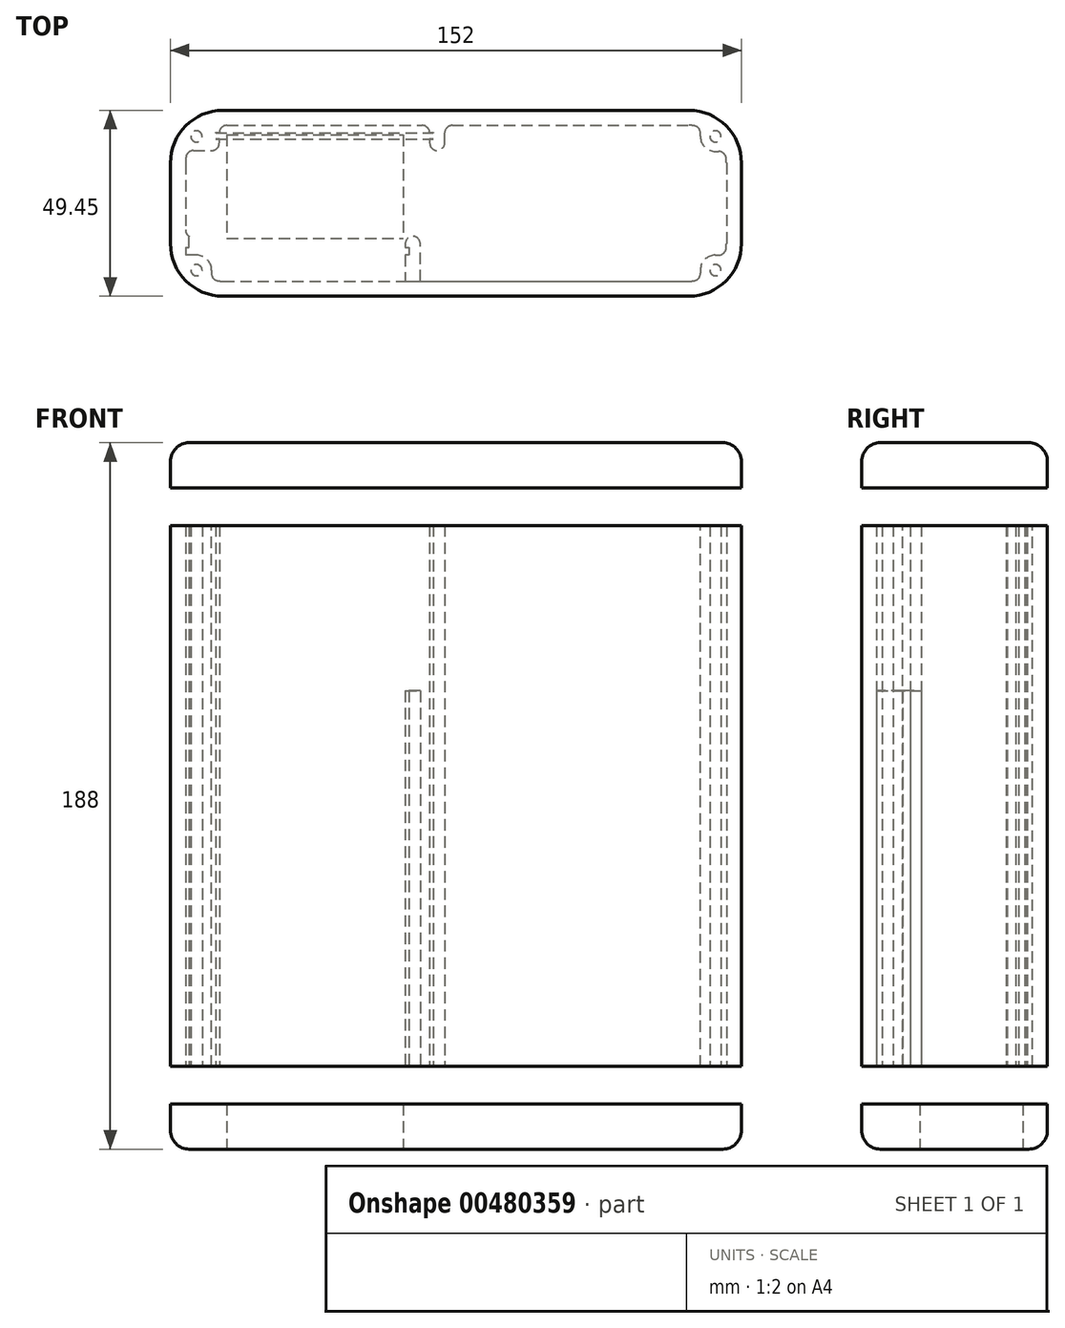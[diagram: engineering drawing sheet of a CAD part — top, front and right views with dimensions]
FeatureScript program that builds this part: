
annotation { "Feature Type Name" : "Feature", "Feature Type Description" : "" }
export const myFeature = defineFeature(function(context is Context, id is Id, definition is map)
    precondition{}
    {
        {
            var Q0;
            Q0=qCreatedBy(makeId("Top.planeOp"),FACE);
            var sketch = newSketch(context, id + "F0", { "sketchPlane" : qUnion([Q0])});
            skLineSegment(sketch, "E0.bottom", {"start": v(-110.78, -14.87) * mm, "end": v(-51.28, -14.87) * mm, "construction": true});
            skLineSegment(sketch, "E0.top", {"start": v(-110.78, -16.67) * mm, "end": v(-51.28, -16.67) * mm, "construction": true});
            skLineSegment(sketch, "E0.left", {"start": v(-110.78, -14.87) * mm, "end": v(-110.78, -16.67) * mm});
            skLineSegment(sketch, "E0.right", {"start": v(-51.28, -14.87) * mm, "end": v(-51.28, -16.67) * mm});
            skLineSegment(sketch, "E1.bottom", {"start": v(-100.78, 17.75) * mm, "end": v(23.22, 17.75) * mm});
            skLineSegment(sketch, "E1.top", {"start": v(-100.78, -23.7) * mm, "end": v(23.22, -23.7) * mm});
            skLineSegment(sketch, "E1.left", {"start": v(-110.78, 7.75) * mm, "end": v(-110.78, -13.7) * mm});
            skLineSegment(sketch, "E1.right", {"start": v(33.22, 7.75) * mm, "end": v(33.22, -13.7) * mm});
            skPoint(sketch, "E2", {"position": v(-38.78, -23.7) * mm});
            skPoint(sketch, "E3.visualSharp", {"position": v(-110.78, 17.75) * mm});
            skArc(sketch, "E3.filletArc", {"start": v(-100.78, 17.75) * mm, "mid": v(-107.85, 14.83) * mm, "end": v(-110.78, 7.75) * mm});
            skPoint(sketch, "E4.visualSharp", {"position": v(33.22, 17.75) * mm});
            skArc(sketch, "E4.filletArc", {"start": v(33.22, 7.75) * mm, "mid": v(30.29, 14.83) * mm, "end": v(23.22, 17.75) * mm});
            skPoint(sketch, "E5.visualSharp", {"position": v(33.22, -23.7) * mm});
            skArc(sketch, "E5.filletArc", {"start": v(23.22, -23.7) * mm, "mid": v(30.29, -20.77) * mm, "end": v(33.22, -13.7) * mm});
            skPoint(sketch, "E6.visualSharp", {"position": v(-110.78, -23.7) * mm});
            skArc(sketch, "E6.filletArc", {"start": v(-110.78, -13.7) * mm, "mid": v(-107.85, -20.77) * mm, "end": v(-100.78, -23.7) * mm});
            skLineSegment(sketch, "E7.0", {"start": v(-100.78, 21.75) * mm, "end": v(23.22, 21.75) * mm});
            skArc(sketch, "E7.1", {"start": v(37.22, 7.75) * mm, "mid": v(33.12, 17.65) * mm, "end": v(23.22, 21.75) * mm});
            skArc(sketch, "E7.2", {"start": v(-100.78, 21.75) * mm, "mid": v(-110.68, 17.65) * mm, "end": v(-114.78, 7.75) * mm});
            skLineSegment(sketch, "E7.3", {"start": v(37.22, 7.75) * mm, "end": v(37.22, -13.7) * mm});
            skLineSegment(sketch, "E7.4", {"start": v(-114.78, 7.75) * mm, "end": v(-114.78, -13.7) * mm});
            skArc(sketch, "E7.5", {"start": v(-114.78, -13.7) * mm, "mid": v(-110.68, -23.6) * mm, "end": v(-100.78, -27.7) * mm});
            skLineSegment(sketch, "E7.6", {"start": v(-100.78, -27.7) * mm, "end": v(23.22, -27.7) * mm});
            skArc(sketch, "E7.7", {"start": v(23.22, -27.7) * mm, "mid": v(33.12, -23.6) * mm, "end": v(37.22, -13.7) * mm});
            skPoint(sketch, "E8", {"position": v(-38.78, -12.34) * mm});
            skPoint(sketch, "E9.visualSharp", {"position": v(-107.28, -12.34) * mm});
            skPoint(sketch, "E10.visualSharp", {"position": v(-107.28, -52.34) * mm});
            skPoint(sketch, "E11.visualSharp", {"position": v(29.72, -52.34) * mm});
            skCircle(sketch, "E12", {"center": v(-107.85, 14.83) * mm, "radius": 4 * mm});
            skLineSegment(sketch, "E13", {"start": v(-100.78, 7.75) * mm, "end": v(-110.78, 17.75) * mm, "construction": true});
            skCircle(sketch, "E14", {"center": v(30.29, -20.77) * mm, "radius": 4 * mm});
            skLineSegment(sketch, "E15", {"start": v(23.22, -13.7) * mm, "end": v(33.22, -23.7) * mm, "construction": true});
            skCircle(sketch, "E16", {"center": v(-107.85, -20.77) * mm, "radius": 4 * mm});
            skLineSegment(sketch, "E17", {"start": v(-100.78, -13.7) * mm, "end": v(-110.78, -23.7) * mm, "construction": true});
            skLineSegment(sketch, "E18.bottom", {"start": v(-102.78, 15.75) * mm, "end": v(-44.78, 15.75) * mm});
            skLineSegment(sketch, "E18.top", {"start": v(-102.78, 14.15) * mm, "end": v(-44.78, 14.15) * mm});
            skLineSegment(sketch, "E18.left", {"start": v(-102.78, 15.75) * mm, "end": v(-102.78, 14.15) * mm});
            skLineSegment(sketch, "E18.right", {"start": v(-44.78, 15.75) * mm, "end": v(-44.78, 14.15) * mm});
            skLineSegment(sketch, "E19", {"start": v(-45.78, 17.75) * mm, "end": v(-45.78, 15.85) * mm});
            skLineSegment(sketch, "E20", {"start": v(-45.78, 15.85) * mm, "end": v(-44.78, 15.85) * mm});
            skLineSegment(sketch, "E21", {"start": v(-44.78, 15.85) * mm, "end": v(-44.78, 14.05) * mm});
            skLineSegment(sketch, "E22", {"start": v(-44.78, 14.05) * mm, "end": v(-45.78, 14.05) * mm});
            skLineSegment(sketch, "E23", {"start": v(-45.78, 14.05) * mm, "end": v(-45.78, 11.05) * mm});
            skLineSegment(sketch, "E24", {"start": v(-45.78, 11.05) * mm, "end": v(-41.78, 11.05) * mm});
            skLineSegment(sketch, "E25", {"start": v(-41.78, 11.05) * mm, "end": v(-41.78, 17.75) * mm});
            skPoint(sketch, "E26", {"position": v(-44.78, 14.95) * mm});
            skLineSegment(sketch, "E27", {"start": v(-110.78, 11.05) * mm, "end": v(-101.78, 11.05) * mm});
            skLineSegment(sketch, "E28", {"start": v(-101.78, 11.05) * mm, "end": v(-101.78, 14.05) * mm});
            skLineSegment(sketch, "E29", {"start": v(-101.78, 14.05) * mm, "end": v(-110.78, 14.05) * mm});
            skLineSegment(sketch, "E30", {"start": v(-107.85, -16.77) * mm, "end": v(-110.3, -16.77) * mm});
            skLineSegment(sketch, "E31", {"start": v(-103.85, -20.77) * mm, "end": v(-103.85, -23.22) * mm});
            skLineSegment(sketch, "E32", {"start": v(30.29, -16.77) * mm, "end": v(32.74, -16.77) * mm});
            skLineSegment(sketch, "E33", {"start": v(26.29, -20.77) * mm, "end": v(26.29, -23.22) * mm});
            skLineSegment(sketch, "E34", {"start": v(-110.78, -14.77) * mm, "end": v(-109.78, -14.77) * mm});
            skLineSegment(sketch, "E35", {"start": v(-109.78, -14.77) * mm, "end": v(-109.78, -11.77) * mm});
            skLineSegment(sketch, "E36", {"start": v(-109.78, -11.77) * mm, "end": v(-110.78, -11.77) * mm});
            skLineSegment(sketch, "E37", {"start": v(-110.78, -16.77) * mm, "end": v(-109.78, -16.77) * mm});
            skLineSegment(sketch, "E38", {"start": v(-51.28, -9.75) * mm, "end": v(-51.28, -11.75) * mm});
            skCircle(sketch, "E39", {"center": v(30.29, 14.83) * mm, "radius": 4 * mm});
            skCircle(sketch, "E40", {"center": v(30.29, 14.83) * mm, "radius": 1.5 * mm});
            skCircle(sketch, "E41", {"center": v(-107.85, 14.83) * mm, "radius": 1.5 * mm});
            skCircle(sketch, "E42", {"center": v(-107.85, -20.77) * mm, "radius": 1.5 * mm});
            skCircle(sketch, "E43", {"center": v(30.29, -20.77) * mm, "radius": 1.5 * mm});
            skLineSegment(sketch, "E44", {"start": v(33.22, 17.75) * mm, "end": v(23.22, 7.75) * mm, "construction": true});
            skLineSegment(sketch, "E45", {"start": v(-48.28, -23.7) * mm, "end": v(-48.28, -11.77) * mm});
            skLineSegment(sketch, "E46", {"start": v(-48.28, -11.77) * mm, "end": v(-52.28, -11.77) * mm});
            skLineSegment(sketch, "E47", {"start": v(-52.28, -11.77) * mm, "end": v(-52.28, -14.77) * mm});
            skLineSegment(sketch, "E48", {"start": v(-52.28, -14.77) * mm, "end": v(-51.28, -14.77) * mm});
            skLineSegment(sketch, "E49", {"start": v(-51.28, -14.77) * mm, "end": v(-51.28, -16.77) * mm});
            skLineSegment(sketch, "E50", {"start": v(-51.28, -16.77) * mm, "end": v(-52.28, -16.77) * mm});
            skLineSegment(sketch, "E51", {"start": v(-52.28, -16.77) * mm, "end": v(-52.28, -23.7) * mm});
            skLineSegment(sketch, "E52", {"start": v(26.29, 14.83) * mm, "end": v(26.29, 17.27) * mm});
            skLineSegment(sketch, "E53", {"start": v(30.29, 10.83) * mm, "end": v(32.74, 10.83) * mm});
            skLineSegment(sketch, "E54", {"start": v(-102.78, 14.05) * mm, "end": v(-102.78, 15.85) * mm});
            skLineSegment(sketch, "E55", {"start": v(-110.78, -14.77) * mm, "end": v(-110.78, -16.77) * mm});
            skLineSegment(sketch, "E56", {"start": v(-101.78, 15.85) * mm, "end": v(-101.78, 17.7) * mm});
            skLineSegment(sketch, "E57", {"start": v(-102.78, 15.85) * mm, "end": v(-101.78, 15.85) * mm});
            skSolve(sketch);
        }
        {
            var Q0;
            {var subQ9=sQuery(id+"F0.wireOp",EDGE,"E7.0");Q0=makeQuery(id+"F0.imprint","IMPRINT",FACE,{"disambiguationData":[TD([[makeQuery(id+"F0.imprint","IMPRINT",EDGE,{"derivedFrom":subQ9}),-1.0]])]});}
            var Q1;
            {var subQ0=sQuery(id+"F0.wireOp",EDGE,"E12");var subQ2=sQuery(id+"F0.wireOp",EDGE,"E3.filletArc");var subQ3=makeQuery(id+"F0.imprint","INTERSECT",VERTEX,{"disambiguationData":[OD(0.0)],"derivedFrom":[subQ2,subQ0]});Q1=makeQuery(id+"F0.imprint","IMPRINT",FACE,{"disambiguationData":[TD([[makeQuery(id+"F0.imprint","IMPRINT",EDGE,{"disambiguationData":[TD([[subQ3,-1.0]])],"derivedFrom":subQ2}),-1.0]])]});}
            var Q2;
            {var subQ0=sQuery(id+"F0.wireOp",EDGE,"2W4B9iu8-6ltF-Vtcw-TABt-Mn2br8Ru9iya");Q2=makeQuery(id+"F0.imprint","IMPRINT",FACE,{"disambiguationData":[TD([[makeQuery(id+"F0.imprint","IMPRINT",EDGE,{"derivedFrom":subQ0}),1.0]])]});}
            var Q3;
            {var subQ0=sQuery(id+"F0.wireOp",EDGE,"E12");var subQ2=sQuery(id+"F0.wireOp",EDGE,"E3.filletArc");var subQ8=makeQuery(id+"F0.imprint","INTERSECT",VERTEX,{"disambiguationData":[OD(0.0)],"derivedFrom":[subQ2,subQ0]});Q3=makeQuery(id+"F0.imprint","IMPRINT",FACE,{"disambiguationData":[TD([[makeQuery(id+"F0.imprint","IMPRINT",EDGE,{"disambiguationData":[TD([[subQ8,-1.0]])],"derivedFrom":subQ2}),1.0]])]});}
            var Q4;
            {var subQ0=sQuery(id+"F0.wireOp",EDGE,"aaEoFGYO-67Ow-w31H-SEpQ-SyWXDBz15Rrq");Q4=makeQuery(id+"F0.imprint","IMPRINT",FACE,{"disambiguationData":[TD([[makeQuery(id+"F0.imprint","IMPRINT",EDGE,{"derivedFrom":subQ0}),-1.0]])]});}
            var Q5;
            {var subQ0=sQuery(id+"F0.wireOp",EDGE,"E7.3");Q5=makeQuery(id+"F0.imprint","IMPRINT",FACE,{"disambiguationData":[TD([[makeQuery(id+"F0.imprint","IMPRINT",EDGE,{"derivedFrom":subQ0}),-1.0]])]});}
            var Q6;
            {var subQ0=sQuery(id+"F0.wireOp",EDGE,"E14");var subQ2=sQuery(id+"F0.wireOp",EDGE,"E5.filletArc");var subQ3=makeQuery(id+"F0.imprint","INTERSECT",VERTEX,{"disambiguationData":[OD(0.0)],"derivedFrom":[subQ2,subQ0]});Q6=makeQuery(id+"F0.imprint","IMPRINT",FACE,{"disambiguationData":[TD([[makeQuery(id+"F0.imprint","IMPRINT",EDGE,{"disambiguationData":[TD([[subQ3,-1.0]])],"derivedFrom":subQ2}),-1.0]])]});}
            var Q7;
            {var subQ1=sQuery(id+"F0.wireOp",EDGE,"E14");var subQ6=sQuery(id+"F0.wireOp",EDGE,"E5.filletArc");var subQ7=makeQuery(id+"F0.imprint","INTERSECT",VERTEX,{"disambiguationData":[OD(0.0)],"derivedFrom":[subQ6,subQ1]});Q7=makeQuery(id+"F0.imprint","IMPRINT",FACE,{"disambiguationData":[TD([[makeQuery(id+"F0.imprint","IMPRINT",EDGE,{"disambiguationData":[TD([[subQ7,-1.0]])],"derivedFrom":subQ6}),1.0]])]});}
            var Q8;
            {var subQ9=sQuery(id+"F0.wireOp",EDGE,"E1.top");Q8=makeQuery(id+"F0.imprint","IMPRINT",FACE,{"disambiguationData":[TD([[makeQuery(id+"F0.imprint","IMPRINT",EDGE,{"derivedFrom":subQ9}),-1.0]])]});}
            var Q9;
            {var subQ0=sQuery(id+"F0.wireOp",EDGE,"E16");var subQ2=sQuery(id+"F0.wireOp",EDGE,"E6.filletArc");var subQ3=makeQuery(id+"F0.imprint","INTERSECT",VERTEX,{"disambiguationData":[OD(0.0)],"derivedFrom":[subQ2,subQ0]});Q9=makeQuery(id+"F0.imprint","IMPRINT",FACE,{"disambiguationData":[TD([[makeQuery(id+"F0.imprint","IMPRINT",EDGE,{"disambiguationData":[TD([[subQ3,-1.0]])],"derivedFrom":subQ2}),-1.0]])]});}
            var Q10;
            {var subQ0=sQuery(id+"F0.wireOp",EDGE,"E16");var subQ1=sQuery(id+"F0.wireOp",EDGE,"E6.filletArc");var subQ2=makeQuery(id+"F0.imprint","INTERSECT",VERTEX,{"disambiguationData":[OD(0.0)],"derivedFrom":[subQ1,subQ0]});Q10=makeQuery(id+"F0.imprint","IMPRINT",FACE,{"disambiguationData":[TD([[makeQuery(id+"F0.imprint","IMPRINT",EDGE,{"disambiguationData":[TD([[subQ2,-1.0]])],"derivedFrom":subQ1}),1.0]])]});}
            var Q11;
            {var subQ7=sQuery(id+"F0.wireOp",EDGE,"ttZv5H3B-eX0E-SKTf-zCUi-YB3ncVsOdNPo");Q11=makeQuery(id+"F0.imprint","IMPRINT",FACE,{"disambiguationData":[TD([[makeQuery(id+"F0.imprint","IMPRINT",EDGE,{"derivedFrom":subQ7}),-1.0]])]});}
            var Q12;
            {var subQ0=sQuery(id+"F0.wireOp",EDGE,"kMDQpda2-fsvu-s4YW-gm7I-p9UYXz8PP6ZB");Q12=makeQuery(id+"F0.imprint","IMPRINT",FACE,{"disambiguationData":[TD([[makeQuery(id+"F0.imprint","IMPRINT",EDGE,{"derivedFrom":subQ0}),1.0]])]});}
            var Q13;
            {var subQ0=sQuery(id+"F0.wireOp",EDGE,"E37");var subQ1=sQuery(id+"F0.wireOp",EDGE,"E6.filletArc");var subQ2=makeQuery(id+"F0.imprint","INTERSECT",VERTEX,{"derivedFrom":[subQ1,subQ0]});Q13=makeQuery(id+"F0.imprint","IMPRINT",FACE,{"disambiguationData":[TD([[makeQuery(id+"F0.imprint","IMPRINT",EDGE,{"disambiguationData":[TD([[subQ2,-1.0]])],"derivedFrom":subQ1}),1.0]])]});}
            var Q14;
            {var subQ4=sQuery(id+"F0.wireOp",EDGE,"E38");var subQ10=makeQuery(id+"F0.imprint","IMPRINT",VERTEX,{"disambiguationData":[OD(0.0)],"derivedFrom":subQ4});Q14=makeQuery(id+"F0.imprint","IMPRINT",FACE,{"disambiguationData":[TD([[makeQuery(id+"F0.imprint","IMPRINT",EDGE,{"disambiguationData":[TD([[subQ10,-1.0]])],"derivedFrom":subQ4}),1.0]])]});}
            var Q15;
            {var subQ22=sQuery(id+"F0.wireOp",EDGE,"E7.4");Q15=makeQuery(id+"F0.imprint","IMPRINT",FACE,{"disambiguationData":[TD([[makeQuery(id+"F0.imprint","IMPRINT",EDGE,{"derivedFrom":subQ22}),1.0]])]});}
            var Q16;
            {var subQ5=sQuery(id+"F0.wireOp",EDGE,"E18.left");Q16=makeQuery(id+"F0.imprint","IMPRINT",FACE,{"disambiguationData":[TD([[makeQuery(id+"F0.imprint","IMPRINT",EDGE,{"derivedFrom":subQ5}),1.0]])]});}
            var Q17;
            {var subQ3=sQuery(id+"F0.wireOp",EDGE,"E43");var subQ6=sQuery(id+"F0.wireOp",EDGE,"E5.filletArc");var subQ8=makeQuery(id+"F0.imprint","INTERSECT",VERTEX,{"disambiguationData":[OD(1.0)],"derivedFrom":[subQ6,subQ3]});Q17=makeQuery(id+"F0.imprint","IMPRINT",FACE,{"disambiguationData":[TD([[makeQuery(id+"F0.imprint","IMPRINT",EDGE,{"disambiguationData":[TD([[subQ8,-1.0]])],"derivedFrom":subQ6}),1.0]])]});}
            var Q18;
            {var subQ0=sQuery(id+"F0.wireOp",EDGE,"E33");Q18=makeQuery(id+"F0.imprint","IMPRINT",FACE,{"disambiguationData":[TD([[makeQuery(id+"F0.imprint","IMPRINT",EDGE,{"derivedFrom":subQ0}),1.0]])]});}
            var Q19;
            {var subQ0=sQuery(id+"F0.wireOp",EDGE,"mgFHwq9W-Mvvh-XZid-bLKJ-4b42OU44zzW1");var subQ1=sQuery(id+"F0.wireOp",EDGE,"E6.filletArc");var subQ2=makeQuery(id+"F0.imprint","INTERSECT",VERTEX,{"derivedFrom":[subQ1,subQ0]});Q19=makeQuery(id+"F0.imprint","IMPRINT",FACE,{"disambiguationData":[TD([[makeQuery(id+"F0.imprint","IMPRINT",EDGE,{"disambiguationData":[TD([[subQ2,-1.0]])],"derivedFrom":subQ1}),-1.0]])]});}
            var Q20;
            {var subQ0=sQuery(id+"F0.wireOp",EDGE,"E32");Q20=makeQuery(id+"F0.imprint","IMPRINT",FACE,{"disambiguationData":[TD([[makeQuery(id+"F0.imprint","IMPRINT",EDGE,{"derivedFrom":subQ0}),-1.0]])]});}
            var Q21;
            {var subQ0=sQuery(id+"F0.wireOp",EDGE,"E31");Q21=makeQuery(id+"F0.imprint","IMPRINT",FACE,{"disambiguationData":[TD([[makeQuery(id+"F0.imprint","IMPRINT",EDGE,{"derivedFrom":subQ0}),-1.0]])]});}
            var Q22;
            {var subQ0=sQuery(id+"F0.wireOp",EDGE,"E39");var subQ2=sQuery(id+"F0.wireOp",EDGE,"E4.filletArc");var subQ6=makeQuery(id+"F0.imprint","INTERSECT",VERTEX,{"disambiguationData":[OD(0.0)],"derivedFrom":[subQ2,subQ0]});Q22=makeQuery(id+"F0.imprint","IMPRINT",FACE,{"disambiguationData":[TD([[makeQuery(id+"F0.imprint","IMPRINT",EDGE,{"disambiguationData":[TD([[subQ6,-1.0]])],"derivedFrom":subQ2}),-1.0]])]});}
            var Q23;
            {var subQ0=sQuery(id+"F0.wireOp",EDGE,"E39");var subQ1=sQuery(id+"F0.wireOp",EDGE,"E4.filletArc");var subQ2=makeQuery(id+"F0.imprint","INTERSECT",VERTEX,{"disambiguationData":[OD(0.0)],"derivedFrom":[subQ1,subQ0]});Q23=makeQuery(id+"F0.imprint","IMPRINT",FACE,{"disambiguationData":[TD([[makeQuery(id+"F0.imprint","IMPRINT",EDGE,{"disambiguationData":[TD([[subQ2,-1.0]])],"derivedFrom":subQ1}),1.0]])]});}
            var Q24;
            {var subQ0=sQuery(id+"F0.wireOp",EDGE,"E52");Q24=makeQuery(id+"F0.imprint","IMPRINT",FACE,{"disambiguationData":[TD([[makeQuery(id+"F0.imprint","IMPRINT",EDGE,{"derivedFrom":subQ0}),-1.0]])]});}
            var Q25;
            {var subQ0=sQuery(id+"F0.wireOp",EDGE,"E53");Q25=makeQuery(id+"F0.imprint","IMPRINT",FACE,{"disambiguationData":[TD([[makeQuery(id+"F0.imprint","IMPRINT",EDGE,{"derivedFrom":subQ0}),1.0]])]});}
            var Q26;
            {var subQ0=sQuery(id+"F0.wireOp",EDGE,"E35");Q26=makeQuery(id+"F0.imprint","IMPRINT",FACE,{"disambiguationData":[TD([[makeQuery(id+"F0.imprint","IMPRINT",EDGE,{"derivedFrom":subQ0}),1.0]])]});}
            var Q27;
            {var subQ1=sQuery(id+"F0.wireOp",EDGE,"E19");Q27=makeQuery(id+"F0.imprint","IMPRINT",FACE,{"disambiguationData":[TD([[makeQuery(id+"F0.imprint","IMPRINT",EDGE,{"derivedFrom":subQ1}),1.0]])]});}
            var Q28;
            {var subQ0=sQuery(id+"F0.wireOp",EDGE,"E27");Q28=makeQuery(id+"F0.imprint","IMPRINT",FACE,{"disambiguationData":[TD([[makeQuery(id+"F0.imprint","IMPRINT",EDGE,{"derivedFrom":subQ0}),1.0]])]});}
            var Q29;
            {var subQ0=sQuery(id+"F0.wireOp",EDGE,"EnqMPRIF-PQjg-ndfi-68Pk-OZopwU1ppeKb");Q29=makeQuery(id+"F0.imprint","IMPRINT",FACE,{"disambiguationData":[TD([[makeQuery(id+"F0.imprint","IMPRINT",EDGE,{"derivedFrom":subQ0}),1.0]])]});}
            var Q30;
            {var subQ0=sQuery(id+"F0.wireOp",EDGE,"E56");Q30=makeQuery(id+"F0.imprint","IMPRINT",FACE,{"disambiguationData":[TD([[makeQuery(id+"F0.imprint","IMPRINT",EDGE,{"derivedFrom":subQ0}),1.0]])]});}
            var Q31;
            {var subQ1=sQuery(id+"F0.wireOp",EDGE,"E28");Q31=makeQuery(id+"F0.imprint","IMPRINT",FACE,{"disambiguationData":[TD([[makeQuery(id+"F0.imprint","IMPRINT",EDGE,{"derivedFrom":subQ1}),1.0]])]});}
            var Q32;
            {var subQ5=sQuery(id+"F0.wireOp",EDGE,"E3.filletArc");var subQ8=sQuery(id+"F0.wireOp",EDGE,"E41");var subQ9=makeQuery(id+"F0.imprint","INTERSECT",VERTEX,{"disambiguationData":[OD(1.0)],"derivedFrom":[subQ5,subQ8]});Q32=makeQuery(id+"F0.imprint","IMPRINT",FACE,{"disambiguationData":[TD([[makeQuery(id+"F0.imprint","IMPRINT",EDGE,{"disambiguationData":[TD([[subQ9,-1.0]])],"derivedFrom":subQ5}),1.0]])]});}
            extrude(context, id + "F1", {"entities" : qUnion([Q0, Q1, Q2, Q3, Q4, Q5, Q6, Q7, Q8, Q9, Q10, Q11, Q12, Q13, Q14, Q15, Q16, Q17, Q18, Q19, Q20, Q21, Q22, Q23, Q24, Q25, Q26, Q27, Q28, Q29, Q30, Q31, Q32]), "depth" : 144 * mm, "offsetDistance" : 25 * mm});
        }
        {
            var Q0;
            {var subQ1=sQuery(id+"F0.wireOp",EDGE,"E19");Q0=makeQuery(id+"F0.imprint","IMPRINT",FACE,{"disambiguationData":[TD([[makeQuery(id+"F0.imprint","IMPRINT",EDGE,{"derivedFrom":subQ1}),1.0]])]});}
            var Q1;
            {var subQ0=sQuery(id+"F0.wireOp",EDGE,"E27");Q1=makeQuery(id+"F0.imprint","IMPRINT",FACE,{"disambiguationData":[TD([[makeQuery(id+"F0.imprint","IMPRINT",EDGE,{"derivedFrom":subQ0}),1.0]])]});}
            extrude(context, id + "F2", {"entities" : qUnion([Q0, Q1]), "operationType" : NewBodyOperationType.ADD, "depth" : 67 * mm, "offsetDistance" : 25 * mm});
        }
        {
            var Q0;
            {var subQ0=sQuery(id+"F0.wireOp",EDGE,"E45");Q0=makeQuery(id+"F0.imprint","IMPRINT",FACE,{"disambiguationData":[TD([[makeQuery(id+"F0.imprint","IMPRINT",EDGE,{"derivedFrom":subQ0}),1.0]])]});}
            extrude(context, id + "F3", {"entities" : qUnion([Q0]), "operationType" : NewBodyOperationType.ADD, "depth" : 100 * mm, "offsetDistance" : 25 * mm});
        }
        {
            var Q0;
            Q0=makeQuery(id+"F1.opExtrude","CAP_FACE",FACE,{"disambiguationData":[OSD([sQuery(id+"F0.wireOp",EDGE,"ac47ddaa-1ff9-4fb7-91e3-0095d18774f8.0"),sQuery(id+"F0.wireOp",EDGE,"ac47ddaa-1ff9-4fb7-91e3-0095d18774f8.1"),sQuery(id+"F0.wireOp",EDGE,"ac47ddaa-1ff9-4fb7-91e3-0095d18774f8.2"),sQuery(id+"F0.wireOp",EDGE,"23e3ad9c-f10d-46c0-9b1d-762057cb4504"),sQuery(id+"F0.wireOp",EDGE,"20860ca5-1e23-45d1-b3d5-98853785f5a3.filletArc"),sQuery(id+"F0.wireOp",EDGE,"e5807837-fe32-4673-91be-abad1df8b40d.filletArc"),sQuery(id+"F0.wireOp",EDGE,"52051394-9daf-43b8-8cdd-08482cc01996.filletArc"),sQuery(id+"F0.wireOp",EDGE,"ed5e0c1f-c6d5-438c-b0a1-3757e7beccb2.filletArc"),sQuery(id+"F0.wireOp",EDGE,"8e21b9bb-f049-4d82-9402-97ffcd915d1b.0"),sQuery(id+"F0.wireOp",EDGE,"8e21b9bb-f049-4d82-9402-97ffcd915d1b.1"),sQuery(id+"F0.wireOp",EDGE,"8e21b9bb-f049-4d82-9402-97ffcd915d1b.2"),sQuery(id+"F0.wireOp",EDGE,"8e21b9bb-f049-4d82-9402-97ffcd915d1b.3"),sQuery(id+"F0.wireOp",EDGE,"8e21b9bb-f049-4d82-9402-97ffcd915d1b.4"),sQuery(id+"F0.wireOp",EDGE,"8e21b9bb-f049-4d82-9402-97ffcd915d1b.5"),sQuery(id+"F0.wireOp",EDGE,"8e21b9bb-f049-4d82-9402-97ffcd915d1b.6"),sQuery(id+"F0.wireOp",EDGE,"8e21b9bb-f049-4d82-9402-97ffcd915d1b.7")])],"isStart":false});
            var Q1;
            Q1=makeQuery(id+"F1.opExtrude","CAP_FACE",FACE,{"disambiguationData":[OSD([sQuery(id+"F0.wireOp",EDGE,"E1.bottom"),sQuery(id+"F0.wireOp",EDGE,"E1.top"),sQuery(id+"F0.wireOp",EDGE,"E1.left"),sQuery(id+"F0.wireOp",EDGE,"E1.right"),sQuery(id+"F0.wireOp",EDGE,"e5adbce5-5c82-4fed-9f0c-1d366584b07e.0"),sQuery(id+"F0.wireOp",EDGE,"e5adbce5-5c82-4fed-9f0c-1d366584b07e.1"),sQuery(id+"F0.wireOp",EDGE,"e5adbce5-5c82-4fed-9f0c-1d366584b07e.2"),sQuery(id+"F0.wireOp",EDGE,"e5adbce5-5c82-4fed-9f0c-1d366584b07e.3")])],"isStart":false});
            cPlane(context, id + "F4", {"entities" : qUnion([Q0, Q1]), "cplaneType" : CPlaneType.OFFSET, "offset" : 10 * mm, "width" : 150 * mm, "height" : 150 * mm});
        }
        {
            var Q0;
            Q0=qCreatedBy(id+"F4.planeOp",FACE);
            var sketch = newSketch(context, id + "F5", { "sketchPlane" : qUnion([Q0])});
            skLineSegment(sketch, "E58.0", {"start": v(-100.78, 21.75) * mm, "end": v(23.22, 21.75) * mm});
            skArc(sketch, "E58.1", {"start": v(-100.78, 21.75) * mm, "mid": v(-110.68, 17.65) * mm, "end": v(-114.78, 7.75) * mm});
            skLineSegment(sketch, "E58.2", {"start": v(-114.78, 7.75) * mm, "end": v(-114.78, -13.7) * mm});
            skArc(sketch, "E58.3", {"start": v(-114.78, -13.7) * mm, "mid": v(-110.68, -23.6) * mm, "end": v(-100.78, -27.7) * mm});
            skLineSegment(sketch, "E58.4", {"start": v(-100.78, -27.7) * mm, "end": v(23.22, -27.7) * mm});
            skArc(sketch, "E58.5", {"start": v(23.22, -27.7) * mm, "mid": v(33.12, -23.6) * mm, "end": v(37.22, -13.7) * mm});
            skLineSegment(sketch, "E58.6", {"start": v(37.22, 7.75) * mm, "end": v(37.22, -13.7) * mm});
            skArc(sketch, "E58.7", {"start": v(37.22, 7.75) * mm, "mid": v(33.12, 17.65) * mm, "end": v(23.22, 21.75) * mm});
            skSolve(sketch);
        }
        {
            var Q0;
            Q0=makeQuery(id+"F1.opExtrude","CAP_FACE",FACE,{"disambiguationData":[OSD([sQuery(id+"F0.wireOp",EDGE,"ac47ddaa-1ff9-4fb7-91e3-0095d18774f8.0"),sQuery(id+"F0.wireOp",EDGE,"ac47ddaa-1ff9-4fb7-91e3-0095d18774f8.1"),sQuery(id+"F0.wireOp",EDGE,"ac47ddaa-1ff9-4fb7-91e3-0095d18774f8.2"),sQuery(id+"F0.wireOp",EDGE,"23e3ad9c-f10d-46c0-9b1d-762057cb4504"),sQuery(id+"F0.wireOp",EDGE,"20860ca5-1e23-45d1-b3d5-98853785f5a3.filletArc"),sQuery(id+"F0.wireOp",EDGE,"e5807837-fe32-4673-91be-abad1df8b40d.filletArc"),sQuery(id+"F0.wireOp",EDGE,"52051394-9daf-43b8-8cdd-08482cc01996.filletArc"),sQuery(id+"F0.wireOp",EDGE,"ed5e0c1f-c6d5-438c-b0a1-3757e7beccb2.filletArc"),sQuery(id+"F0.wireOp",EDGE,"8e21b9bb-f049-4d82-9402-97ffcd915d1b.0"),sQuery(id+"F0.wireOp",EDGE,"8e21b9bb-f049-4d82-9402-97ffcd915d1b.1"),sQuery(id+"F0.wireOp",EDGE,"8e21b9bb-f049-4d82-9402-97ffcd915d1b.2"),sQuery(id+"F0.wireOp",EDGE,"8e21b9bb-f049-4d82-9402-97ffcd915d1b.3"),sQuery(id+"F0.wireOp",EDGE,"8e21b9bb-f049-4d82-9402-97ffcd915d1b.4"),sQuery(id+"F0.wireOp",EDGE,"8e21b9bb-f049-4d82-9402-97ffcd915d1b.5"),sQuery(id+"F0.wireOp",EDGE,"8e21b9bb-f049-4d82-9402-97ffcd915d1b.6"),sQuery(id+"F0.wireOp",EDGE,"8e21b9bb-f049-4d82-9402-97ffcd915d1b.7")])],"isStart":true});
            var Q1;
            Q1=makeQuery(id+"F0.imprint","IMPRINT",FACE,{"disambiguationData":[TD([[makeQuery(id+"F0.imprint","IMPRINT",EDGE,{"derivedFrom":sQuery(id+"F0.wireOp",EDGE,"E1.bottom")}),1.0]])]});
            cPlane(context, id + "F6", {"entities" : qUnion([Q0, Q1]), "cplaneType" : CPlaneType.OFFSET, "offset" : 10 * mm, "oppositeDirection" : true, "width" : 150 * mm, "height" : 150 * mm});
        }
        {
            var Q0;
            Q0=qCreatedBy(id+"F6.planeOp",FACE);
            var sketch = newSketch(context, id + "F7", { "sketchPlane" : qUnion([Q0])});
            skArc(sketch, "E59.0", {"start": v(-114.78, -13.7) * mm, "mid": v(-110.68, -23.6) * mm, "end": v(-100.78, -27.7) * mm});
            skLineSegment(sketch, "E59.1", {"start": v(-100.78, -27.7) * mm, "end": v(23.22, -27.7) * mm});
            skArc(sketch, "E59.2", {"start": v(23.22, -27.7) * mm, "mid": v(33.12, -23.6) * mm, "end": v(37.22, -13.7) * mm});
            skLineSegment(sketch, "E59.3", {"start": v(37.22, 7.75) * mm, "end": v(37.22, -13.7) * mm});
            skArc(sketch, "E59.4", {"start": v(37.22, 7.75) * mm, "mid": v(33.12, 17.65) * mm, "end": v(23.22, 21.75) * mm});
            skLineSegment(sketch, "E59.5", {"start": v(-100.78, 21.75) * mm, "end": v(23.22, 21.75) * mm});
            skArc(sketch, "E59.6", {"start": v(-100.78, 21.75) * mm, "mid": v(-110.68, 17.65) * mm, "end": v(-114.78, 7.75) * mm});
            skLineSegment(sketch, "E59.7", {"start": v(-114.78, 7.75) * mm, "end": v(-114.78, -13.7) * mm});
            skSolve(sketch);
        }
        {
            var Q0;
            Q0 = qSketchRegion(id + "F7", true);
            extrude(context, id + "F8", {"entities" : qUnion([Q0]), "oppositeDirection" : true, "depth" : 12 * mm, "offsetDistance" : 25 * mm});
        }
        {
            var Q0;
            Q0 = qSketchRegion(id + "F5", true);
            extrude(context, id + "F9", {"entities" : qUnion([Q0]), "depth" : 12 * mm, "offsetDistance" : 25 * mm});
        }
        {
            var Q0;
            Q0=makeQuery(id+"F9.opExtrude","CAP_FACE",FACE,{"disambiguationData":[OSD([sQuery(id+"F5.wireOp",EDGE,"E58.0"),sQuery(id+"F5.wireOp",EDGE,"E58.1"),sQuery(id+"F5.wireOp",EDGE,"E58.2"),sQuery(id+"F5.wireOp",EDGE,"E58.3"),sQuery(id+"F5.wireOp",EDGE,"E58.4"),sQuery(id+"F5.wireOp",EDGE,"E58.5"),sQuery(id+"F5.wireOp",EDGE,"E58.6"),sQuery(id+"F5.wireOp",EDGE,"E58.7")])],"isStart":false});
            var Q1;
            Q1=makeQuery(id+"F8.opExtrude","CAP_FACE",FACE,{"disambiguationData":[OSD([sQuery(id+"F7.wireOp",EDGE,"E59.0"),sQuery(id+"F7.wireOp",EDGE,"E59.1"),sQuery(id+"F7.wireOp",EDGE,"E59.2"),sQuery(id+"F7.wireOp",EDGE,"E59.3"),sQuery(id+"F7.wireOp",EDGE,"E59.4"),sQuery(id+"F7.wireOp",EDGE,"E59.5"),sQuery(id+"F7.wireOp",EDGE,"E59.6"),sQuery(id+"F7.wireOp",EDGE,"E59.7")])],"isStart":false});
            fillet(context, id + "F10", {"entities" : qUnion([Q0, Q1]), "radius" : 5 * mm, "tangentPropagation" : true, "allowEdgeOverflow" : false});
        }
        {
            var Q0;
            Q0=makeQuery(id+"F2.opExtrude","SWEPT_EDGE",EDGE,{"disambiguationData":[OSD([sQuery(id+"F0.wireOp",EDGE,"E24"),sQuery(id+"F0.wireOp",EDGE,"E25")])]});
            var Q1;
            Q1=makeQuery(id+"F2.opExtrude","SWEPT_EDGE",EDGE,{"disambiguationData":[OSD([sQuery(id+"F0.wireOp",EDGE,"E45"),sQuery(id+"F0.wireOp",EDGE,"E46")])]});
            var Q2;
            Q2=makeQuery(id+"F2.opExtrude","SWEPT_EDGE",EDGE,{"disambiguationData":[OSD([sQuery(id+"F0.wireOp",EDGE,"E46"),sQuery(id+"F0.wireOp",EDGE,"E47")])]});
            var Q3;
            Q3=makeQuery(id+"F2.opExtrude","SWEPT_EDGE",EDGE,{"disambiguationData":[OSD([sQuery(id+"F0.wireOp",EDGE,"E23"),sQuery(id+"F0.wireOp",EDGE,"E24")])]});
            var Q4;
            Q4=makeQuery(id+"F2.opExtrude","SWEPT_EDGE",EDGE,{"disambiguationData":[OSD([sQuery(id+"F0.wireOp",EDGE,"E1.left"),sQuery(id+"F0.wireOp",EDGE,"E36")])]});
            var Q5;
            Q5=makeQuery(id+"F2.opExtrude","SWEPT_EDGE",EDGE,{"disambiguationData":[OSD([sQuery(id+"F0.wireOp",EDGE,"E1.left"),sQuery(id+"F0.wireOp",EDGE,"E27")])]});
            var Q6;
            Q6=makeQuery(id+"F2.opExtrude","SWEPT_EDGE",EDGE,{"disambiguationData":[OSD([sQuery(id+"F0.wireOp",EDGE,"E1.top"),sQuery(id+"F0.wireOp",EDGE,"E45")])]});
            var Q7;
            Q7=makeQuery(id+"F2.opExtrude","SWEPT_EDGE",EDGE,{"disambiguationData":[OSD([sQuery(id+"F0.wireOp",EDGE,"E1.top"),sQuery(id+"F0.wireOp",EDGE,"E51")])]});
            var Q8;
            Q8=makeQuery(id+"F2.opExtrude","SWEPT_EDGE",EDGE,{"disambiguationData":[OSD([sQuery(id+"F0.wireOp",EDGE,"E1.bottom"),sQuery(id+"F0.wireOp",EDGE,"E19")])]});
            var Q9;
            Q9=makeQuery(id+"F2.opExtrude","SWEPT_EDGE",EDGE,{"disambiguationData":[OSD([sQuery(id+"F0.wireOp",EDGE,"E1.bottom"),sQuery(id+"F0.wireOp",EDGE,"E25")])]});
            var Q10;
            Q10=makeQuery(id+"F1.opExtrude","SWEPT_EDGE",EDGE,{"disambiguationData":[OSD([sQuery(id+"F0.wireOp",EDGE,"E3.filletArc"),sQuery(id+"F0.wireOp",EDGE,"2W4B9iu8-6ltF-Vtcw-TABt-Mn2br8Ru9iya")])]});
            var Q11;
            Q11=makeQuery(id+"F1.opExtrude","SWEPT_EDGE",EDGE,{"disambiguationData":[OSD([sQuery(id+"F0.wireOp",EDGE,"E6.filletArc"),sQuery(id+"F0.wireOp",EDGE,"E31")])]});
            var Q12;
            Q12=makeQuery(id+"F1.opExtrude","SWEPT_EDGE",EDGE,{"disambiguationData":[OSD([sQuery(id+"F0.wireOp",EDGE,"E5.filletArc"),sQuery(id+"F0.wireOp",EDGE,"E33")])]});
            var Q13;
            Q13=makeQuery(id+"F1.opExtrude","SWEPT_EDGE",EDGE,{"disambiguationData":[OSD([sQuery(id+"F0.wireOp",EDGE,"E5.filletArc"),sQuery(id+"F0.wireOp",EDGE,"E32")])]});
            var Q14;
            Q14=makeQuery(id+"F1.opExtrude","SWEPT_EDGE",EDGE,{"disambiguationData":[OSD([sQuery(id+"F0.wireOp",EDGE,"E4.filletArc"),sQuery(id+"F0.wireOp",EDGE,"E53")])]});
            var Q15;
            Q15=makeQuery(id+"F1.opExtrude","SWEPT_EDGE",EDGE,{"disambiguationData":[OSD([sQuery(id+"F0.wireOp",EDGE,"E4.filletArc"),sQuery(id+"F0.wireOp",EDGE,"E52")])]});
            var Q16;
            Q16=makeQuery(id+"F1.opExtrude","SWEPT_EDGE",EDGE,{"disambiguationData":[OSD([sQuery(id+"F0.wireOp",EDGE,"E45"),sQuery(id+"F0.wireOp",EDGE,"E46")])]});
            var Q17;
            Q17=makeQuery(id+"F1.opExtrude","SWEPT_EDGE",EDGE,{"disambiguationData":[OSD([sQuery(id+"F0.wireOp",EDGE,"E1.top"),sQuery(id+"F0.wireOp",EDGE,"E45")])]});
            var Q18;
            Q18=makeQuery(id+"F1.opExtrude","SWEPT_EDGE",EDGE,{"disambiguationData":[OSD([sQuery(id+"F0.wireOp",EDGE,"E1.top"),sQuery(id+"F0.wireOp",EDGE,"E51")])]});
            var Q19;
            Q19=makeQuery(id+"F1.opExtrude","SWEPT_EDGE",EDGE,{"disambiguationData":[OSD([sQuery(id+"F0.wireOp",EDGE,"E46"),sQuery(id+"F0.wireOp",EDGE,"E47")])]});
            var Q20;
            Q20=makeQuery(id+"F1.opExtrude","SWEPT_EDGE",EDGE,{"disambiguationData":[OSD([sQuery(id+"F0.wireOp",EDGE,"E1.left"),sQuery(id+"F0.wireOp",EDGE,"E36")])]});
            var Q21;
            Q21=makeQuery(id+"F3.opExtrude","SWEPT_EDGE",EDGE,{"disambiguationData":[OSD([sQuery(id+"F0.wireOp",EDGE,"E46"),sQuery(id+"F0.wireOp",EDGE,"E47")])]});
            var Q22;
            Q22=makeQuery(id+"F3.opExtrude","SWEPT_EDGE",EDGE,{"disambiguationData":[OSD([sQuery(id+"F0.wireOp",EDGE,"E45"),sQuery(id+"F0.wireOp",EDGE,"E46")])]});
            var Q23;
            Q23=makeQuery(id+"F3.opExtrude","SWEPT_EDGE",EDGE,{"disambiguationData":[OSD([sQuery(id+"F0.wireOp",EDGE,"E1.top"),sQuery(id+"F0.wireOp",EDGE,"E45")])]});
            var Q24;
            Q24=makeQuery(id+"F3.opExtrude","SWEPT_EDGE",EDGE,{"disambiguationData":[OSD([sQuery(id+"F0.wireOp",EDGE,"E1.top"),sQuery(id+"F0.wireOp",EDGE,"E51")])]});
            var Q25;
            Q25=makeQuery(id+"F1.opExtrude","SWEPT_EDGE",EDGE,{"disambiguationData":[OSD([sQuery(id+"F0.wireOp",EDGE,"E24"),sQuery(id+"F0.wireOp",EDGE,"E25")])]});
            var Q26;
            Q26=makeQuery(id+"F1.opExtrude","SWEPT_EDGE",EDGE,{"disambiguationData":[OSD([sQuery(id+"F0.wireOp",EDGE,"E1.bottom"),sQuery(id+"F0.wireOp",EDGE,"E25")])]});
            var Q27;
            Q27=makeQuery(id+"F1.opExtrude","SWEPT_EDGE",EDGE,{"disambiguationData":[OSD([sQuery(id+"F0.wireOp",EDGE,"E23"),sQuery(id+"F0.wireOp",EDGE,"E24")])]});
            var Q28;
            Q28=makeQuery(id+"F1.opExtrude","SWEPT_EDGE",EDGE,{"disambiguationData":[OSD([sQuery(id+"F0.wireOp",EDGE,"E1.bottom"),sQuery(id+"F0.wireOp",EDGE,"E19")])]});
            var Q29;
            Q29=makeQuery(id+"F1.opExtrude","SWEPT_EDGE",EDGE,{"disambiguationData":[OSD([sQuery(id+"F0.wireOp",EDGE,"E1.left"),sQuery(id+"F0.wireOp",EDGE,"E27")])]});
            var Q30;
            Q30=makeQuery(id+"F1.opExtrude","SWEPT_EDGE",EDGE,{"disambiguationData":[OSD([sQuery(id+"F0.wireOp",EDGE,"E27"),sQuery(id+"F0.wireOp",EDGE,"E28")])]});
            fillet(context, id + "F11", {"entities" : qUnion([Q0, Q1, Q2, Q3, Q4, Q5, Q6, Q7, Q8, Q9, Q10, Q11, Q12, Q13, Q14, Q15, Q16, Q17, Q18, Q19, Q20, Q21, Q22, Q23, Q24, Q25, Q26, Q27, Q28, Q29, Q30]), "radius" : 2 * mm, "tangentPropagation" : true, "allowEdgeOverflow" : false});
        }
        {
            var Q0;
            Q0=makeQuery(id+"F8.opExtrude","CAP_FACE",FACE,{"disambiguationData":[OSD([sQuery(id+"F7.wireOp",EDGE,"E59.0"),sQuery(id+"F7.wireOp",EDGE,"E59.1"),sQuery(id+"F7.wireOp",EDGE,"E59.2"),sQuery(id+"F7.wireOp",EDGE,"E59.3"),sQuery(id+"F7.wireOp",EDGE,"E59.4"),sQuery(id+"F7.wireOp",EDGE,"E59.5"),sQuery(id+"F7.wireOp",EDGE,"E59.6"),sQuery(id+"F7.wireOp",EDGE,"E59.7")])],"isStart":false});
            var sketch = newSketch(context, id + "F12", { "sketchPlane" : qUnion([Q0])});
            skLineSegment(sketch, "E60.bottom", {"start": v(-99.78, -15.25) * mm, "end": v(-52.78, -15.25) * mm});
            skLineSegment(sketch, "E60.top", {"start": v(-99.78, 12.25) * mm, "end": v(-52.78, 12.25) * mm});
            skLineSegment(sketch, "E60.left", {"start": v(-99.78, -15.25) * mm, "end": v(-99.78, 12.25) * mm});
            skLineSegment(sketch, "E60.right", {"start": v(-52.78, -15.25) * mm, "end": v(-52.78, 12.25) * mm});
            skSolve(sketch);
        }
        {
            var Q0;
            Q0 = qSketchRegion(id + "F12", true);
            extrude(context, id + "F13", {"entities" : qUnion([Q0]), "operationType" : NewBodyOperationType.REMOVE, "endBound" : BoundingType.UP_TO_NEXT, "oppositeDirection" : true, "depth" : 25 * mm, "offsetDistance" : 25 * mm});
        }
    });
